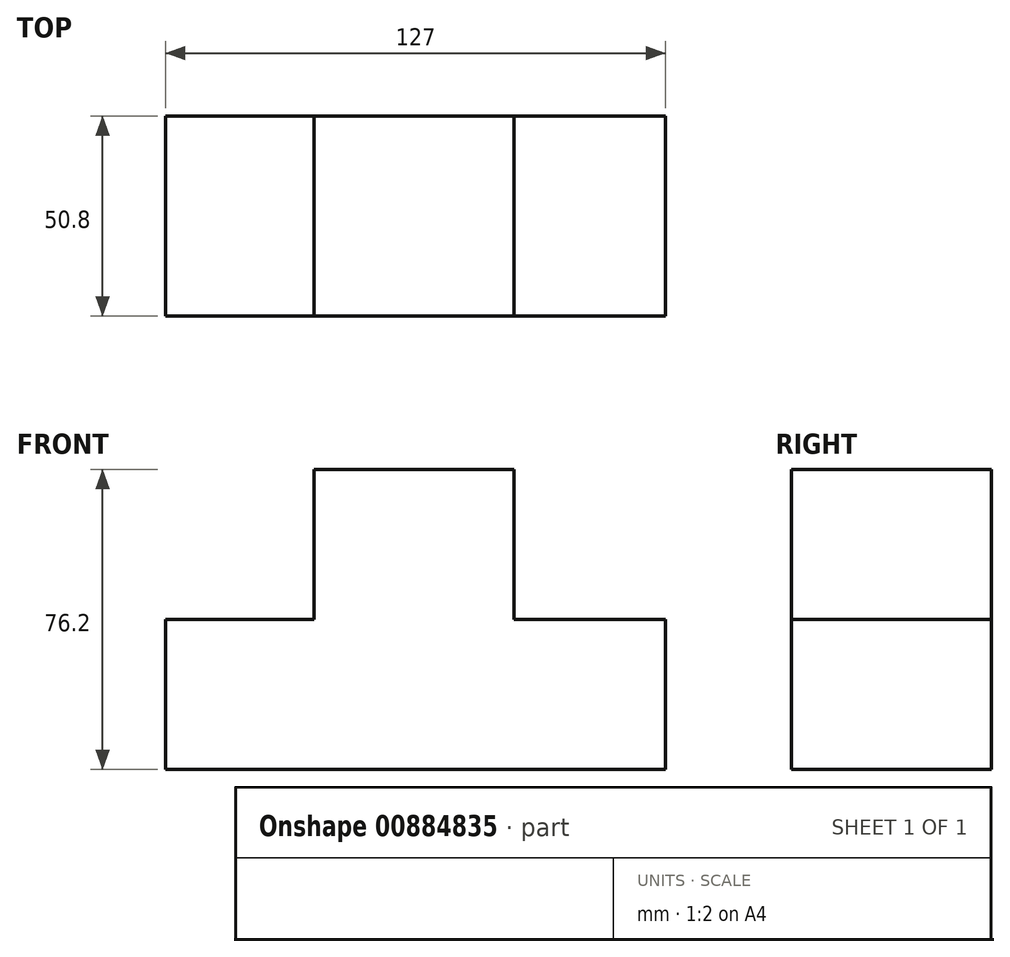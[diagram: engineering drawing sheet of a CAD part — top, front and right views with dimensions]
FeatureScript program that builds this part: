
annotation { "Feature Type Name" : "Feature", "Feature Type Description" : "" }
export const myFeature = defineFeature(function(context is Context, id is Id, definition is map)
    precondition{}
    {
        {
            var Q0;
            Q0=qCreatedBy(makeId("Front.planeOp"),FACE);
            var sketch = newSketch(context, id + "F0", { "sketchPlane" : qUnion([Q0])});
            skLineSegment(sketch, "E0.bottom", {"start": v(63.5, -19.05) * mm, "end": v(-63.5, -19.05) * mm});
            skLineSegment(sketch, "E0.top", {"start": v(63.5, 19.05) * mm, "end": v(-63.5, 19.05) * mm});
            skLineSegment(sketch, "E0.left", {"start": v(63.5, -19.05) * mm, "end": v(63.5, 19.05) * mm});
            skLineSegment(sketch, "E0.right", {"start": v(-63.5, -19.05) * mm, "end": v(-63.5, 19.05) * mm});
            skPoint(sketch, "E0.middle", {"position": v(0, 0) * mm});
            skLineSegment(sketch, "E1.bottom", {"start": v(-25.74, 57.15) * mm, "end": v(25.06, 57.15) * mm});
            skLineSegment(sketch, "E1.left", {"start": v(-25.74, 57.15) * mm, "end": v(-25.74, 19.05) * mm});
            skLineSegment(sketch, "E1.right", {"start": v(25.06, 57.15) * mm, "end": v(25.06, 19.05) * mm});
            skPoint(sketch, "E1.top.end.orphan", {"position": v(25.74, -57.15) * mm});
            skPoint(sketch, "E2.trimOffspring.end.orphan", {"position": v(-25.06, -57.15) * mm});
            skSolve(sketch);
        }
        {
            var Q0;
            Q0 = qSketchRegion(id + "F0", true);
            extrude(context, id + "F1", {"entities" : qUnion([Q0]), "depth" : 50.8 * mm, "offsetDistance" : 25.4 * mm});
        }
    });
